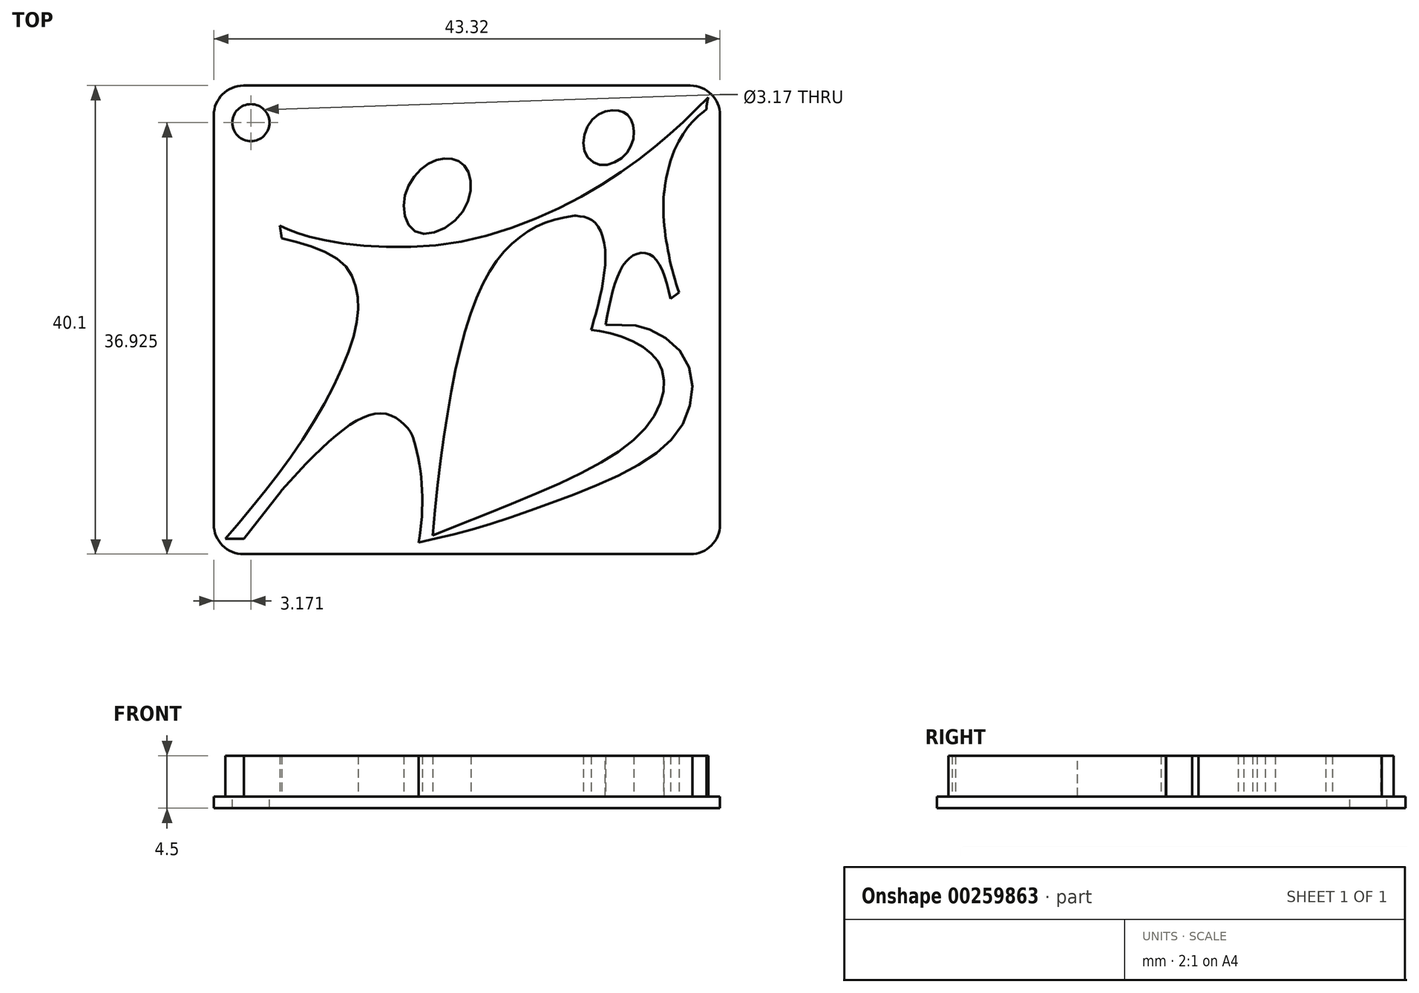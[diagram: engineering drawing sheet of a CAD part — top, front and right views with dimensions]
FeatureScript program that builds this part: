
annotation { "Feature Type Name" : "Feature", "Feature Type Description" : "" }
export const myFeature = defineFeature(function(context is Context, id is Id, definition is map)
    precondition{}
    {
        {
            var Q0;
            Q0=qCreatedBy(makeId("Top.planeOp"),FACE);
            var sketch = newSketch(context, id + "F0", { "sketchPlane" : qUnion([Q0])});
            skSolve(sketch);
        }
        {
            var Q0;
            Q0=qCreatedBy(makeId("Top.planeOp"),FACE);
            var sketch = newSketch(context, id + "F1", { "sketchPlane" : qUnion([Q0])});
            skLineSegment(sketch, "E0", {"start": v(-22.23, -15.3) * mm, "end": v(-20.65, -15.3) * mm});
            skLineSegment(sketch, "E1", {"start": v(-20.65, -15.3) * mm, "end": v(-17.45, -11.2) * mm});
            skFitSpline(sketch, "E2", {"points": [v(-17.45, -11.2) * mm, v(-8.51, -4.63) * mm, v(-6.14, -6.75) * mm, v(-7.07, -6.8) * mm], "startDerivative": vector(19.75, 21.9) * mm, "endDerivative": vector(-15.69, 8.33) * mm});
            skArc(sketch, "E3", {"start": v(-5.72, -15.63) * mm, "mid": v(-5.4, -11.17) * mm, "end": v(-6.14, -6.75) * mm});
            skFitSpline(sketch, "E4", {"points": [v(-5.72, -15.63) * mm, v(-0.92, -14.47) * mm, v(5.1, -12.44) * mm, v(12.73, -9.22) * mm, v(17.05, -5.18) * mm, v(17.17, 0) * mm, v(13.47, 2.8) * mm, v(10.3, 3) * mm], "startDerivative": vector(34.78, 7.68) * mm, "endDerivative": vector(-38.22, 1.94) * mm});
            skFitSpline(sketch, "E5", {"points": [v(10.3, 3) * mm, v(11.39, 7.3) * mm, v(12.53, 8.85) * mm, v(13.69, 9.14) * mm, v(14.78, 8.36) * mm, v(15.86, 5.23) * mm], "startDerivative": vector(3.36, 17.25) * mm, "endDerivative": vector(3.7, -15.07) * mm});
            skLineSegment(sketch, "E6", {"start": v(15.86, 5.23) * mm, "end": v(16.6, 5.76) * mm});
            skFitSpline(sketch, "E7", {"points": [v(16.6, 5.76) * mm, v(15.38, 14.9) * mm], "startDerivative": vector(-2.98, 8.18) * mm, "endDerivative": vector(1.32, 7.42) * mm});
            skFitSpline(sketch, "E8", {"points": [v(15.38, 14.9) * mm, v(18.94, 21.45) * mm], "startDerivative": vector(1.84, 13.75) * mm, "endDerivative": vector(1.32, 1.18) * mm});
            skArc(sketch, "E9", {"start": v(19.1, 22.47) * mm, "mid": v(18.97, 21.97) * mm, "end": v(18.94, 21.45) * mm});
            skFitSpline(sketch, "E10", {"points": [v(19.1, 22.47) * mm, v(12.12, 16.4) * mm, v(-2.4, 10.06) * mm, v(-14.73, 10.44) * mm, v(-17.58, 11.48) * mm], "startDerivative": vector(-23.65, -23.54) * mm, "endDerivative": vector(-15.68, 7.56) * mm});
            skLineSegment(sketch, "E11", {"start": v(-17.58, 11.48) * mm, "end": v(-17.43, 10.39) * mm});
            skFitSpline(sketch, "E12", {"points": [v(-17.43, 10.39) * mm, v(-12.47, 8.5) * mm, v(-11, 5.86) * mm, v(-11.35, 1.72) * mm, v(-15.54, -6.69) * mm, v(-22.23, -15.3) * mm], "startDerivative": vector(29.21, -6.18) * mm, "endDerivative": vector(-26.72, -31.44) * mm});
            skFitSpline(sketch, "E13", {"points": [v(-2.86, 17.2) * mm, v(-5.12, 16.63) * mm, v(-6.97, 13.58) * mm, v(-5.75, 10.9) * mm, v(-1.99, 12.57) * mm, v(-1.47, 16.11) * mm, v(-2.86, 17.2) * mm]});
            skFitSpline(sketch, "E14", {"points": [v(11.4, 21.33) * mm, v(9.51, 20.88) * mm, v(8.4, 18.4) * mm, v(9.53, 16.75) * mm, v(11.7, 17.3) * mm, v(12.72, 19.32) * mm, v(12.28, 20.84) * mm, v(11.4, 21.33) * mm]});
            skFitSpline(sketch, "E15", {"points": [v(7.7, 12.33) * mm, v(3.55, 10.92) * mm, v(-0.48, 5.92) * mm, v(-4.5, -15.03) * mm], "startDerivative": vector(-21.48, -2.27) * mm, "endDerivative": vector(-4.46, -50.03) * mm});
            skFitSpline(sketch, "E16", {"points": [v(-4.5, -15.03) * mm, v(13.37, -6.23) * mm, v(15.2, -1.16) * mm, v(12.95, 1.42) * mm, v(9.07, 2.56) * mm], "startDerivative": vector(52.64, 21.5) * mm, "endDerivative": vector(-13.98, 0.35) * mm});
            skFitSpline(sketch, "E17", {"points": [v(7.7, 12.33) * mm, v(9.23, 11.89) * mm, v(10.27, 9.07) * mm, v(9.48, 4.05) * mm, v(9.07, 2.56) * mm], "startDerivative": vector(8.36, -0.77) * mm, "endDerivative": vector(-1.72, -6.4) * mm});
            skSolve(sketch);
        }
        {
            var Q0;
            Q0 = qSketchRegion(id + "F1", true);
            extrude(context, id + "F2", {"entities" : qUnion([Q0]), "depth" : 3.5 * mm});
        }
        {
            var Q0;
            Q0=makeQuery(id+"F2.opExtrude","SWEPT_EDGE",EDGE,{"disambiguationData":[OSD([sQuery(id+"F1.wireOp",EDGE,"E2"),sQuery(id+"F1.wireOp",EDGE,"E3")])]});
            var Q1;
            Q1=makeQuery(id+"F2.opExtrude","SWEPT_EDGE",EDGE,{"disambiguationData":[OSD([sQuery(id+"F1.wireOp",EDGE,"E1"),sQuery(id+"F1.wireOp",EDGE,"E2")])]});
            var Q2;
            Q2=makeQuery(id+"F2.opExtrude","SWEPT_EDGE",EDGE,{"disambiguationData":[OSD([sQuery(id+"F1.wireOp",EDGE,"E7"),sQuery(id+"F1.wireOp",EDGE,"E8")])]});
            var Q3;
            Q3=makeQuery(id+"F2.opExtrude","SWEPT_EDGE",EDGE,{"disambiguationData":[OSD([sQuery(id+"F1.wireOp",EDGE,"E15"),sQuery(id+"F1.wireOp",EDGE,"E17")])]});
            fillet(context, id + "F3", {"entities" : qUnion([Q0, Q1, Q2, Q3]), "radius" : .5 * mm, "tangentPropagation" : true, "allowEdgeOverflow" : false});
        }
        {
            var Q0;
            Q0=makeQuery(id+"F2.opExtrude","CAP_FACE",FACE,{"disambiguationData":[OSD([sQuery(id+"F1.wireOp",EDGE,"E0"),sQuery(id+"F1.wireOp",EDGE,"E1"),sQuery(id+"F1.wireOp",EDGE,"E2"),sQuery(id+"F1.wireOp",EDGE,"E3"),sQuery(id+"F1.wireOp",EDGE,"E4"),sQuery(id+"F1.wireOp",EDGE,"E5"),sQuery(id+"F1.wireOp",EDGE,"E6"),sQuery(id+"F1.wireOp",EDGE,"E7"),sQuery(id+"F1.wireOp",EDGE,"E8"),sQuery(id+"F1.wireOp",EDGE,"E9"),sQuery(id+"F1.wireOp",EDGE,"E10"),sQuery(id+"F1.wireOp",EDGE,"E11"),sQuery(id+"F1.wireOp",EDGE,"E12"),sQuery(id+"F1.wireOp",EDGE,"E15"),sQuery(id+"F1.wireOp",EDGE,"E16"),sQuery(id+"F1.wireOp",EDGE,"E17")])],"isStart":true});
            var sketch = newSketch(context, id + "F4", { "sketchPlane" : qUnion([Q0])});
            skLineSegment(sketch, "E18.bottom", {"start": v(20.1, -23.47) * mm, "end": v(-23.23, -23.47) * mm});
            skLineSegment(sketch, "E18.top", {"start": v(20.1, 16.63) * mm, "end": v(-23.23, 16.63) * mm});
            skLineSegment(sketch, "E18.left", {"start": v(20.1, -23.47) * mm, "end": v(20.1, 16.63) * mm});
            skLineSegment(sketch, "E18.right", {"start": v(-23.23, -23.47) * mm, "end": v(-23.23, 16.63) * mm});
            skSolve(sketch);
        }
        {
            var Q0;
            Q0 = qSketchRegion(id + "F4", true);
            extrude(context, id + "F5", {"entities" : qUnion([Q0]), "operationType" : NewBodyOperationType.ADD, "depth" : 1 * mm});
        }
        {
            var Q0;
            Q0=makeQuery(id+"F5.opExtrude","SWEPT_EDGE",EDGE,{"disambiguationData":[OSD([sQuery(id+"F4.wireOp",EDGE,"E18.top"),sQuery(id+"F4.wireOp",EDGE,"E18.left")])]});
            var Q1;
            Q1=makeQuery(id+"F5.opExtrude","SWEPT_EDGE",EDGE,{"disambiguationData":[OSD([sQuery(id+"F4.wireOp",EDGE,"E18.bottom"),sQuery(id+"F4.wireOp",EDGE,"E18.left")])]});
            var Q2;
            Q2=makeQuery(id+"F5.opExtrude","SWEPT_EDGE",EDGE,{"disambiguationData":[OSD([sQuery(id+"F4.wireOp",EDGE,"E18.top"),sQuery(id+"F4.wireOp",EDGE,"E18.right")])]});
            var Q3;
            Q3=makeQuery(id+"F5.opExtrude","SWEPT_EDGE",EDGE,{"disambiguationData":[OSD([sQuery(id+"F4.wireOp",EDGE,"E18.bottom"),sQuery(id+"F4.wireOp",EDGE,"E18.right")])]});
            fillet(context, id + "F6", {"entities" : qUnion([Q0, Q1, Q2, Q3]), "radius" : 2.54 * mm, "tangentPropagation" : true, "allowEdgeOverflow" : false});
        }
        {
            var Q0;
            {var subQ1=sQuery(id+"F4.wireOp",EDGE,"E18.top");var subQ6=sQuery(id+"F4.wireOp",EDGE,"E18.right");var subQ7=sQuery(id+"F4.wireOp",EDGE,"E18.bottom");var subQ8=sQuery(id+"F4.wireOp",EDGE,"E18.left");Q0=makeQuery(id+"F5.boolean.opBoolean","SPLIT",FACE,{"disambiguationData":[TD([makeQuery(id+"F2.opExtrude","SWEPT_FACE",FACE,{"disambiguationData":[OSD([sQuery(id+"F1.wireOp",EDGE,"E0")])]})])],"derivedFrom":makeQuery(id+"F5.opExtrude","CAP_FACE",FACE,{"disambiguationData":[OSD([subQ7,subQ1,subQ8,subQ6])],"isStart":true})});}
            var sketch = newSketch(context, id + "F7", { "sketchPlane" : qUnion([Q0])});
            skCircle(sketch, "E19", {"center": v(-20.06, 20.3) * mm, "radius": 1.59 * mm});
            skSolve(sketch);
        }
        {
            var Q0;
            Q0 = qSketchRegion(id + "F7", true);
            extrude(context, id + "F8", {"entities" : qUnion([Q0]), "operationType" : NewBodyOperationType.REMOVE, "endBound" : BoundingType.THROUGH_ALL, "oppositeDirection" : true, "depth" : 25.4 * mm});
        }
    });
